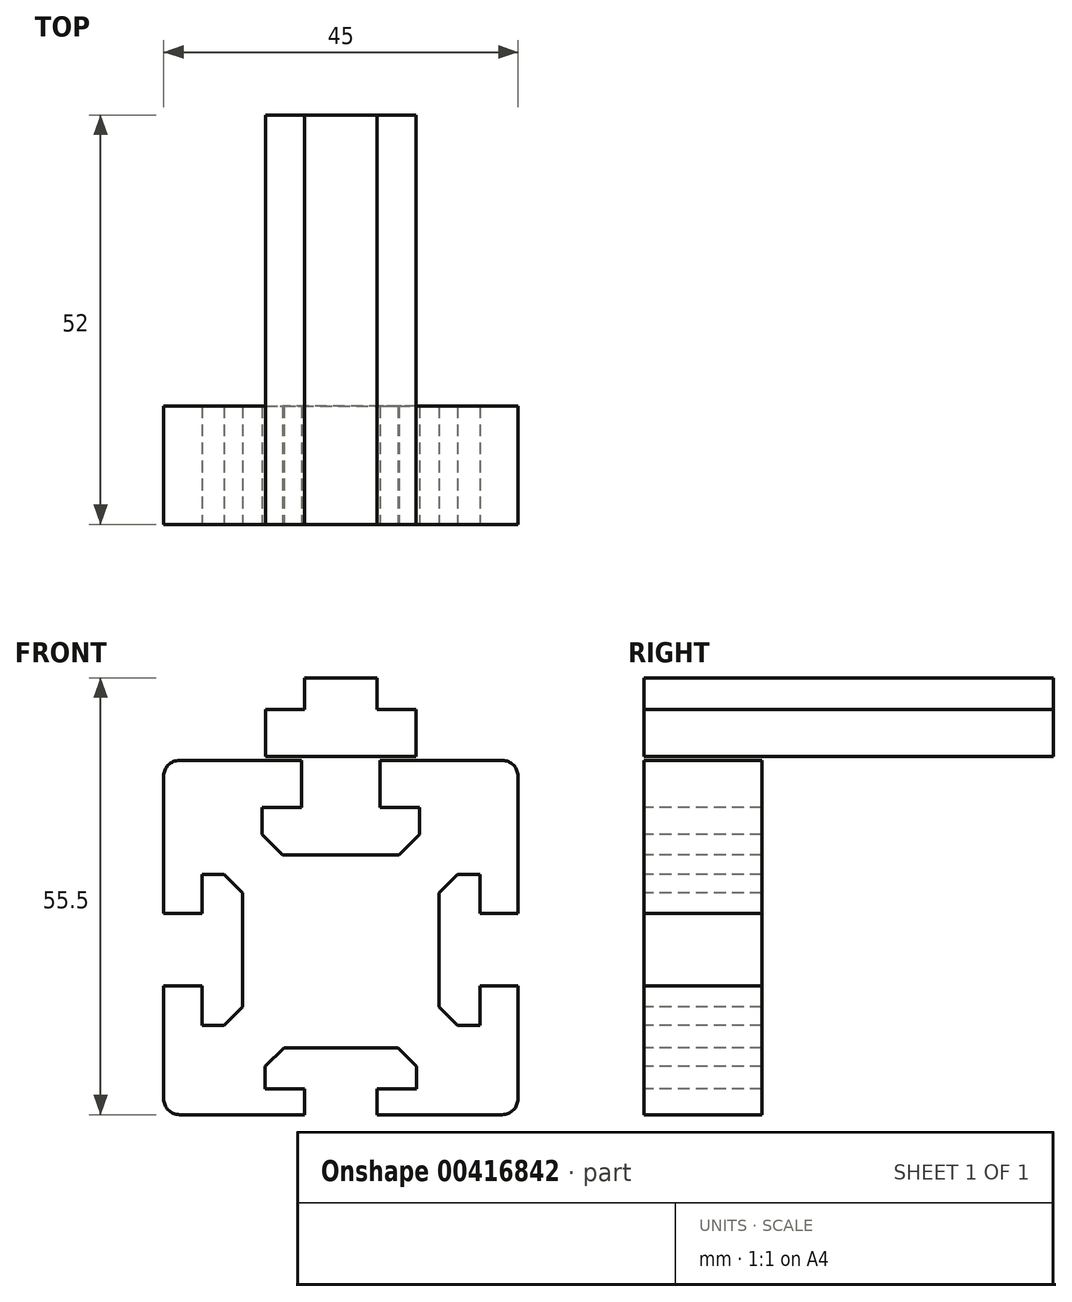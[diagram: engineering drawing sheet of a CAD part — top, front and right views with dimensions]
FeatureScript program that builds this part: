
annotation { "Feature Type Name" : "Feature", "Feature Type Description" : "" }
export const myFeature = defineFeature(function(context is Context, id is Id, definition is map)
    precondition{}
    {
        {
            var Q0;
            Q0=qCreatedBy(makeId("Front.planeOp"),FACE);
            var sketch = newSketch(context, id + "F0", { "sketchPlane" : qUnion([Q0])});
            skLineSegment(sketch, "E0.bottom", {"start": v(0, 0) * mm, "end": v(45, 0) * mm});
            skLineSegment(sketch, "E0.top", {"start": v(0, 45) * mm, "end": v(45, 45) * mm});
            skLineSegment(sketch, "E0.left", {"start": v(0, 0) * mm, "end": v(0, 45) * mm});
            skLineSegment(sketch, "E0.right", {"start": v(45, 0) * mm, "end": v(45, 45) * mm});
            skLineSegment(sketch, "E1.bottom", {"start": v(32.5, 45) * mm, "end": v(12.5, 45) * mm});
            skLineSegment(sketch, "E1.top", {"start": v(29.9, 33) * mm, "end": v(15.1, 33) * mm});
            skLineSegment(sketch, "E1.left", {"start": v(32.5, 39) * mm, "end": v(32.5, 35.6) * mm});
            skLineSegment(sketch, "E1.right", {"start": v(12.5, 39) * mm, "end": v(12.5, 35.6) * mm});
            skPoint(sketch, "E1.middle", {"position": v(22.5, 39) * mm});
            skPoint(sketch, "E1.middle.positionSnap0", {"position": v(22.5, 45) * mm});
            skPoint(sketch, "E1.centerSnap0", {"position": v(22.5, 45) * mm});
            skPoint(sketch, "E2.middle", {"position": v(22.5, 20.94) * mm});
            skLineSegment(sketch, "E3.bottom", {"start": v(12.5, 45) * mm, "end": v(17.5, 45) * mm});
            skLineSegment(sketch, "E3.top", {"start": v(12.5, 39) * mm, "end": v(17.5, 39) * mm});
            skLineSegment(sketch, "E3.right", {"start": v(17.5, 45) * mm, "end": v(17.5, 39) * mm});
            skLineSegment(sketch, "E4.bottom", {"start": v(32.5, 45) * mm, "end": v(27.5, 45) * mm});
            skLineSegment(sketch, "E4.top", {"start": v(32.5, 39) * mm, "end": v(27.5, 39) * mm});
            skLineSegment(sketch, "E4.right", {"start": v(27.5, 45) * mm, "end": v(27.5, 39) * mm});
            skLineSegment(sketch, "E5", {"start": v(12.5, 35.6) * mm, "end": v(15.1, 33) * mm});
            skLineSegment(sketch, "E6", {"start": v(22.5, 51.72) * mm, "end": v(22.5, 53.38) * mm, "construction": true});
            skLineSegment(sketch, "E7.MirrorCS", {"start": v(32.5, 35.6) * mm, "end": v(29.9, 33) * mm});
            skPoint(sketch, "E8.orphan", {"position": v(12.5, 33) * mm});
            skPoint(sketch, "E9.orphan", {"position": v(32.5, 33) * mm});
            skLineSegment(sketch, "E10.0", {"start": v(17.9, 45) * mm, "end": v(17.9, 38.6) * mm});
            skLineSegment(sketch, "E10.1", {"start": v(12.9, 38.6) * mm, "end": v(17.9, 38.6) * mm});
            skLineSegment(sketch, "E10.2", {"start": v(12.9, 38.6) * mm, "end": v(12.9, 35.77) * mm});
            skLineSegment(sketch, "E10.3", {"start": v(12.9, 35.77) * mm, "end": v(15.27, 33.4) * mm});
            skLineSegment(sketch, "E10.4", {"start": v(29.73, 33.4) * mm, "end": v(15.27, 33.4) * mm});
            skLineSegment(sketch, "E10.5", {"start": v(27.1, 45) * mm, "end": v(27.1, 38.6) * mm});
            skLineSegment(sketch, "E10.6", {"start": v(32.1, 38.6) * mm, "end": v(27.1, 38.6) * mm});
            skLineSegment(sketch, "E10.7", {"start": v(32.1, 38.6) * mm, "end": v(32.1, 35.77) * mm});
            skLineSegment(sketch, "E10.8", {"start": v(32.1, 35.77) * mm, "end": v(29.73, 33.4) * mm});
            skLineSegment(sketch, "E11", {"start": v(17.9, 38.6) * mm, "end": v(27.1, 38.6) * mm});
            skLineSegment(sketch, "E12.bottom", {"start": v(17.9, 45) * mm, "end": v(27.1, 45) * mm});
            skLineSegment(sketch, "E12.top", {"start": v(17.9, 55.5) * mm, "end": v(27.1, 55.5) * mm});
            skLineSegment(sketch, "E12.left", {"start": v(17.9, 45) * mm, "end": v(17.9, 55.5) * mm});
            skLineSegment(sketch, "E12.right", {"start": v(27.1, 45) * mm, "end": v(27.1, 55.5) * mm});
            skLineSegment(sketch, "E13.bottom", {"start": v(32.06, 45.5) * mm, "end": v(12.94, 45.5) * mm});
            skLineSegment(sketch, "E13.top", {"start": v(32.06, 51.5) * mm, "end": v(12.94, 51.5) * mm});
            skLineSegment(sketch, "E13.left", {"start": v(32.06, 45.5) * mm, "end": v(32.06, 51.5) * mm});
            skLineSegment(sketch, "E13.right", {"start": v(12.94, 45.5) * mm, "end": v(12.94, 51.5) * mm});
            skPoint(sketch, "E13.middle", {"position": v(22.5, 48.5) * mm});
            skSolve(sketch);
        }
        {
            var Q0;
            Q0=makeQuery(id+"F0.imprint","IMPRINT",FACE,{"disambiguationData":[TD([[makeQuery(id+"F0.imprint","IMPRINT",EDGE,{"derivedFrom":sQuery(id+"F0.wireOp",EDGE,"E0.bottom")}),1.0]])]});
            extrude(context, id + "F1", {"entities" : qUnion([Q0]), "oppositeDirection" : true, "depth" : 15 * mm});
        }
        {
            var Q0;
            {var subQ0=sQuery(id+"F0.wireOp",EDGE,"E10.0");Q0=makeQuery(id+"F0.imprint","IMPRINT",FACE,{"disambiguationData":[TD([[makeQuery(id+"F0.imprint","IMPRINT",EDGE,{"derivedFrom":subQ0}),1.0]])]});}
            var Q1;
            Q1=makeQuery(id+"F0.imprint","IMPRINT",FACE,{"disambiguationData":[TD([[makeQuery(id+"F0.imprint","IMPRINT",EDGE,{"derivedFrom":sQuery(id+"F0.wireOp",EDGE,"E10.1")}),-1.0]])]});
            var Q2;
            Q2=makeQuery(id+"F0.imprint","IMPRINT",FACE,{"disambiguationData":[TD([[makeQuery(id+"F0.imprint","IMPRINT",EDGE,{"derivedFrom":sQuery(id+"F0.wireOp",EDGE,"E12.bottom")}),1.0]])]});
            var Q3;
            {var subQ5=sQuery(id+"F0.wireOp",EDGE,"E13.left");Q3=makeQuery(id+"F0.imprint","IMPRINT",FACE,{"disambiguationData":[TD([[makeQuery(id+"F0.imprint","IMPRINT",EDGE,{"derivedFrom":subQ5}),1.0]])]});}
            var Q4;
            {var subQ0=sQuery(id+"F0.wireOp",EDGE,"E13.bottom");var subQ1=sQuery(id+"F0.wireOp",EDGE,"E12.left");var subQ2=makeQuery(id+"F0.imprint","INTERSECT",VERTEX,{"derivedFrom":[subQ1,subQ0]});Q4=makeQuery(id+"F0.imprint","IMPRINT",FACE,{"disambiguationData":[TD([[makeQuery(id+"F0.imprint","IMPRINT",EDGE,{"disambiguationData":[TD([[subQ2,-1.0]])],"derivedFrom":subQ1}),-1.0]])]});}
            var Q5;
            {var subQ5=sQuery(id+"F0.wireOp",EDGE,"E13.right");Q5=makeQuery(id+"F0.imprint","IMPRINT",FACE,{"disambiguationData":[TD([[makeQuery(id+"F0.imprint","IMPRINT",EDGE,{"derivedFrom":subQ5}),-1.0]])]});}
            var Q6;
            {var subQ0=sQuery(id+"F0.wireOp",EDGE,"E12.top");Q6=makeQuery(id+"F0.imprint","IMPRINT",FACE,{"disambiguationData":[TD([[makeQuery(id+"F0.imprint","IMPRINT",EDGE,{"derivedFrom":subQ0}),-1.0]])]});}
            extrude(context, id + "F2", {"entities" : qUnion([Q0, Q1, Q2, Q3, Q4, Q5, Q6]), "oppositeDirection" : true, "depth" : 23 * mm});
        }
        {
            var Q0;
            Q0=makeQuery(id+"F2.opExtrude","CAP_FACE",FACE,{"disambiguationData":[OSD([sQuery(id+"F0.wireOp",EDGE,"E10.0"),sQuery(id+"F0.wireOp",EDGE,"E10.1"),sQuery(id+"F0.wireOp",EDGE,"E10.2"),sQuery(id+"F0.wireOp",EDGE,"E10.3"),sQuery(id+"F0.wireOp",EDGE,"E10.4"),sQuery(id+"F0.wireOp",EDGE,"E10.5"),sQuery(id+"F0.wireOp",EDGE,"E10.6"),sQuery(id+"F0.wireOp",EDGE,"E10.7"),sQuery(id+"F0.wireOp",EDGE,"E10.8"),sQuery(id+"F0.wireOp",EDGE,"E12.top"),sQuery(id+"F0.wireOp",EDGE,"E12.left"),sQuery(id+"F0.wireOp",EDGE,"E12.right"),sQuery(id+"F0.wireOp",EDGE,"E13.bottom"),sQuery(id+"F0.wireOp",EDGE,"E13.top"),sQuery(id+"F0.wireOp",EDGE,"E13.left"),sQuery(id+"F0.wireOp",EDGE,"E13.right")])],"isStart":false});
            cPlane(context, id + "F3", {"entities" : qUnion([Q0]), "cplaneType" : CPlaneType.OFFSET, "offset" : 12.5 * mm, "width" : 150 * mm, "height" : 150 * mm});
        }
        {
            var Q0;
            {var subQ0=sQuery(id+"F0.wireOp",EDGE,"E12.bottom");Q0=makeQuery(id+"F0.imprint","IMPRINT",FACE,{"disambiguationData":[TD([[makeQuery(id+"F0.imprint","IMPRINT",EDGE,{"derivedFrom":subQ0}),1.0]])]});}
            var Q1;
            {var subQ0=sQuery(id+"F0.wireOp",EDGE,"E13.bottom");var subQ1=sQuery(id+"F0.wireOp",EDGE,"E12.left");var subQ2=makeQuery(id+"F0.imprint","INTERSECT",VERTEX,{"derivedFrom":[subQ1,subQ0]});Q1=makeQuery(id+"F0.imprint","IMPRINT",FACE,{"disambiguationData":[TD([[makeQuery(id+"F0.imprint","IMPRINT",EDGE,{"disambiguationData":[TD([[subQ2,-1.0]])],"derivedFrom":subQ1}),-1.0]])]});}
            var Q2;
            {var subQ5=sQuery(id+"F0.wireOp",EDGE,"E13.right");Q2=makeQuery(id+"F0.imprint","IMPRINT",FACE,{"disambiguationData":[TD([[makeQuery(id+"F0.imprint","IMPRINT",EDGE,{"derivedFrom":subQ5}),-1.0]])]});}
            var Q3;
            {var subQ5=sQuery(id+"F0.wireOp",EDGE,"E13.left");Q3=makeQuery(id+"F0.imprint","IMPRINT",FACE,{"disambiguationData":[TD([[makeQuery(id+"F0.imprint","IMPRINT",EDGE,{"derivedFrom":subQ5}),1.0]])]});}
            var Q4;
            {var subQ0=sQuery(id+"F0.wireOp",EDGE,"E12.top");Q4=makeQuery(id+"F0.imprint","IMPRINT",FACE,{"disambiguationData":[TD([[makeQuery(id+"F0.imprint","IMPRINT",EDGE,{"derivedFrom":subQ0}),-1.0]])]});}
            var Q5;
            Q5=makeQuery(id+"FNx0hqmUwpef70i_1.opPattern","COPY",FACE,{"derivedFrom":makeQuery(id+"F2.opExtrude","CAP_FACE",FACE,{"disambiguationData":[OSD([sQuery(id+"F0.wireOp",EDGE,"E10.0"),sQuery(id+"F0.wireOp",EDGE,"E10.1"),sQuery(id+"F0.wireOp",EDGE,"E10.2"),sQuery(id+"F0.wireOp",EDGE,"E10.3"),sQuery(id+"F0.wireOp",EDGE,"E10.4"),sQuery(id+"F0.wireOp",EDGE,"E10.5"),sQuery(id+"F0.wireOp",EDGE,"E10.6"),sQuery(id+"F0.wireOp",EDGE,"E10.7"),sQuery(id+"F0.wireOp",EDGE,"E10.8"),sQuery(id+"F0.wireOp",EDGE,"E12.top"),sQuery(id+"F0.wireOp",EDGE,"E12.left"),sQuery(id+"F0.wireOp",EDGE,"E12.right"),sQuery(id+"F0.wireOp",EDGE,"E13.bottom"),sQuery(id+"F0.wireOp",EDGE,"E13.top"),sQuery(id+"F0.wireOp",EDGE,"E13.left"),sQuery(id+"F0.wireOp",EDGE,"E13.right")])],"isStart":false}),"instanceName":"1"});
            var Q6;
            Q6=makeQuery(id+"F2.opExtrude","CAP_FACE",FACE,{"disambiguationData":[OSD([sQuery(id+"F0.wireOp",EDGE,"E10.0"),sQuery(id+"F0.wireOp",EDGE,"E10.1"),sQuery(id+"F0.wireOp",EDGE,"E10.2"),sQuery(id+"F0.wireOp",EDGE,"E10.3"),sQuery(id+"F0.wireOp",EDGE,"E10.4"),sQuery(id+"F0.wireOp",EDGE,"E10.5"),sQuery(id+"F0.wireOp",EDGE,"E10.6"),sQuery(id+"F0.wireOp",EDGE,"E10.7"),sQuery(id+"F0.wireOp",EDGE,"E10.8"),sQuery(id+"F0.wireOp",EDGE,"E12.top"),sQuery(id+"F0.wireOp",EDGE,"E12.left"),sQuery(id+"F0.wireOp",EDGE,"E12.right"),sQuery(id+"F0.wireOp",EDGE,"E13.bottom"),sQuery(id+"F0.wireOp",EDGE,"E13.top"),sQuery(id+"F0.wireOp",EDGE,"E13.left"),sQuery(id+"F0.wireOp",EDGE,"E13.right")])],"isStart":false});
            extrude(context, id + "F4", {"entities" : qUnion([Q0, Q1, Q2, Q3, Q4]), "operationType" : NewBodyOperationType.ADD, "oppositeDirection" : true, "endBoundEntityFace" : qUnion([Q5]), "depth" : 52 * mm});
        }
        {
            var Q0;
            {var subQ0=sQuery(id+"F0.wireOp",EDGE,"E12.top");var subQ1=makeQuery(id+"F2.opExtrude","SWEPT_FACE",FACE,{"disambiguationData":[OSD([subQ0])]});Q0=makeQuery(id+"F4.boolean.opBoolean","MERGE",FACE,{"derivedFrom":[subQ1,makeQuery(id+"FNx0hqmUwpef70i_1.opPattern","COPY",FACE,{"derivedFrom":subQ1,"instanceName":"1"}),makeQuery(id+"F4.opExtrude","SWEPT_FACE",FACE,{"disambiguationData":[OSD([subQ0])]})]});}
            var sketch = newSketch(context, id + "F5", { "sketchPlane" : qUnion([Q0])});
            skLineSegment(sketch, "E14", {"start": v(-53.54, 52) * mm, "end": v(-53.54, 0) * mm});
            skPoint(sketch, "E15", {"position": v(22.5, 26) * mm});
            skPoint(sketch, "E15.positionSnap0", {"position": v(22.5, 0) * mm});
            skPoint(sketch, "E15.positionSnap1", {"position": v(-53.54, 26) * mm});
            skSolve(sketch);
        }
        {
            var Q0;
            Q0=sQuery(id+"F5.wireOp",VERTEX,"E15");
            var Q1;
            Q1=makeQuery(id+"F2.opExtrude","SWEPT_BODY",BODY,{"disambiguationData":[OSD([sQuery(id+"F0.wireOp",EDGE,"E10.0"),sQuery(id+"F0.wireOp",EDGE,"E10.1"),sQuery(id+"F0.wireOp",EDGE,"E10.2"),sQuery(id+"F0.wireOp",EDGE,"E10.3"),sQuery(id+"F0.wireOp",EDGE,"E10.4"),sQuery(id+"F0.wireOp",EDGE,"E10.5"),sQuery(id+"F0.wireOp",EDGE,"E10.6"),sQuery(id+"F0.wireOp",EDGE,"E10.7"),sQuery(id+"F0.wireOp",EDGE,"E10.8"),sQuery(id+"F0.wireOp",EDGE,"E12.top"),sQuery(id+"F0.wireOp",EDGE,"E12.left"),sQuery(id+"F0.wireOp",EDGE,"E12.right"),sQuery(id+"F0.wireOp",EDGE,"E13.bottom"),sQuery(id+"F0.wireOp",EDGE,"E13.top"),sQuery(id+"F0.wireOp",EDGE,"E13.left"),sQuery(id+"F0.wireOp",EDGE,"E13.right")])]});
            var Q2;
            Q2=makeQuery(id+"F1.opExtrude","SWEPT_BODY",BODY,{"disambiguationData":[OSD([sQuery(id+"F0.wireOp",EDGE,"E0.bottom"),sQuery(id+"F0.wireOp",EDGE,"E0.top"),sQuery(id+"F0.wireOp",EDGE,"E0.left"),sQuery(id+"F0.wireOp",EDGE,"E0.right"),sQuery(id+"F0.wireOp",EDGE,"E1.top"),sQuery(id+"F0.wireOp",EDGE,"E1.left"),sQuery(id+"F0.wireOp",EDGE,"E1.right"),sQuery(id+"F0.wireOp",EDGE,"E3.bottom"),sQuery(id+"F0.wireOp",EDGE,"E3.top"),sQuery(id+"F0.wireOp",EDGE,"E3.right"),sQuery(id+"F0.wireOp",EDGE,"E4.bottom"),sQuery(id+"F0.wireOp",EDGE,"E4.top"),sQuery(id+"F0.wireOp",EDGE,"E4.right"),sQuery(id+"F0.wireOp",EDGE,"E5"),sQuery(id+"F0.wireOp",EDGE,"E7.MirrorCS")])]});
            hole(context, id + "F6", {"style" : HoleStyle.SIMPLE, "endStyle" : HoleEndStyle.THROUGH, "standardTappedOrClearance" : lookupTablePath({ "standard" : "ISO", "engagement" : "75%", "pitch" : "1 mm", "size" : "M6", "type" : "Tapped" }), "standardBlindInLast" : lookupTablePath({ "standard" : "ISO", "engagement" : "75%", "pitch" : "1 mm", "size" : "M6", "type" : "Tapped" }), "holeDiameter" : 5 * mm, "showTappedDepth" : true, "tappedDepth" : 15 * mm, "tapClearance" : 0, "locations" : qUnion([Q0]), "scope" : qUnion([Q1, Q2]), "majorDiameter" : 6 * mm});
        }
        {
            var Q0;
            Q0=makeQuery(id+"F1.opExtrude","SWEPT_EDGE",EDGE,{"disambiguationData":[OSD([sQuery(id+"F0.wireOp",EDGE,"E0.top"),sQuery(id+"F0.wireOp",EDGE,"E0.left")])]});
            var Q1;
            Q1=makeQuery(id+"F1.opExtrude","SWEPT_EDGE",EDGE,{"disambiguationData":[OSD([sQuery(id+"F0.wireOp",EDGE,"E0.top"),sQuery(id+"F0.wireOp",EDGE,"E0.right")])]});
            var Q2;
            Q2=makeQuery(id+"F1.opExtrude","SWEPT_EDGE",EDGE,{"disambiguationData":[OSD([sQuery(id+"F0.wireOp",EDGE,"E0.bottom"),sQuery(id+"F0.wireOp",EDGE,"E0.right")])]});
            var Q3;
            Q3=makeQuery(id+"F1.opExtrude","SWEPT_EDGE",EDGE,{"disambiguationData":[OSD([sQuery(id+"F0.wireOp",EDGE,"E0.bottom"),sQuery(id+"F0.wireOp",EDGE,"E0.left")])]});
            fillet(context, id + "F7", {"entities" : qUnion([Q0, Q1, Q2, Q3]), "radius" : 2 * mm, "tangentPropagation" : true, "allowEdgeOverflow" : false});
        }
        {
            var Q0;
            Q0=sQuery(id+"F0.wireOp",VERTEX,"E2.middle");
            var Q1;
            Q1=qCreatedBy(makeId("Right.planeOp"),FACE);
            cPlane(context, id + "F8", {"entities" : qUnion([Q0, Q1]), "cplaneType" : CPlaneType.PLANE_POINT, "offset" : 25 * mm, "width" : 150 * mm, "height" : 150 * mm});
        }
        {
            var Q0;
            Q0=qCreatedBy(id+"F8.planeOp",FACE);
            var sketch = newSketch(context, id + "F9", { "sketchPlane" : qUnion([Q0])});
            skLineSegment(sketch, "E16", {"start": v(-41.14, 20.94) * mm, "end": v(-78.03, 20.94) * mm});
            skSolve(sketch);
        }
        {
            var Q0;
            Q0=makeQuery(id+"F2.opExtrude","SWEPT_BODY",BODY,{"disambiguationData":[OSD([sQuery(id+"F0.wireOp",EDGE,"E10.0"),sQuery(id+"F0.wireOp",EDGE,"E10.1"),sQuery(id+"F0.wireOp",EDGE,"E10.2"),sQuery(id+"F0.wireOp",EDGE,"E10.3"),sQuery(id+"F0.wireOp",EDGE,"E10.4"),sQuery(id+"F0.wireOp",EDGE,"E10.5"),sQuery(id+"F0.wireOp",EDGE,"E10.6"),sQuery(id+"F0.wireOp",EDGE,"E10.7"),sQuery(id+"F0.wireOp",EDGE,"E10.8"),sQuery(id+"F0.wireOp",EDGE,"E12.top"),sQuery(id+"F0.wireOp",EDGE,"E12.left"),sQuery(id+"F0.wireOp",EDGE,"E12.right"),sQuery(id+"F0.wireOp",EDGE,"E13.bottom"),sQuery(id+"F0.wireOp",EDGE,"E13.top"),sQuery(id+"F0.wireOp",EDGE,"E13.left"),sQuery(id+"F0.wireOp",EDGE,"E13.right")])]});
            var Q1;
            Q1=sQuery(id+"F9.wireOp",EDGE,"E16");
            circularPattern(context, id + "F10", {"operationType" : NewBodyOperationType.REMOVE, "entities" : qUnion([Q0]), "axis" : qUnion([Q1]), "angle" : 360 * degree, "instanceCount" : 4, "equalSpace" : true});
        }
    });
